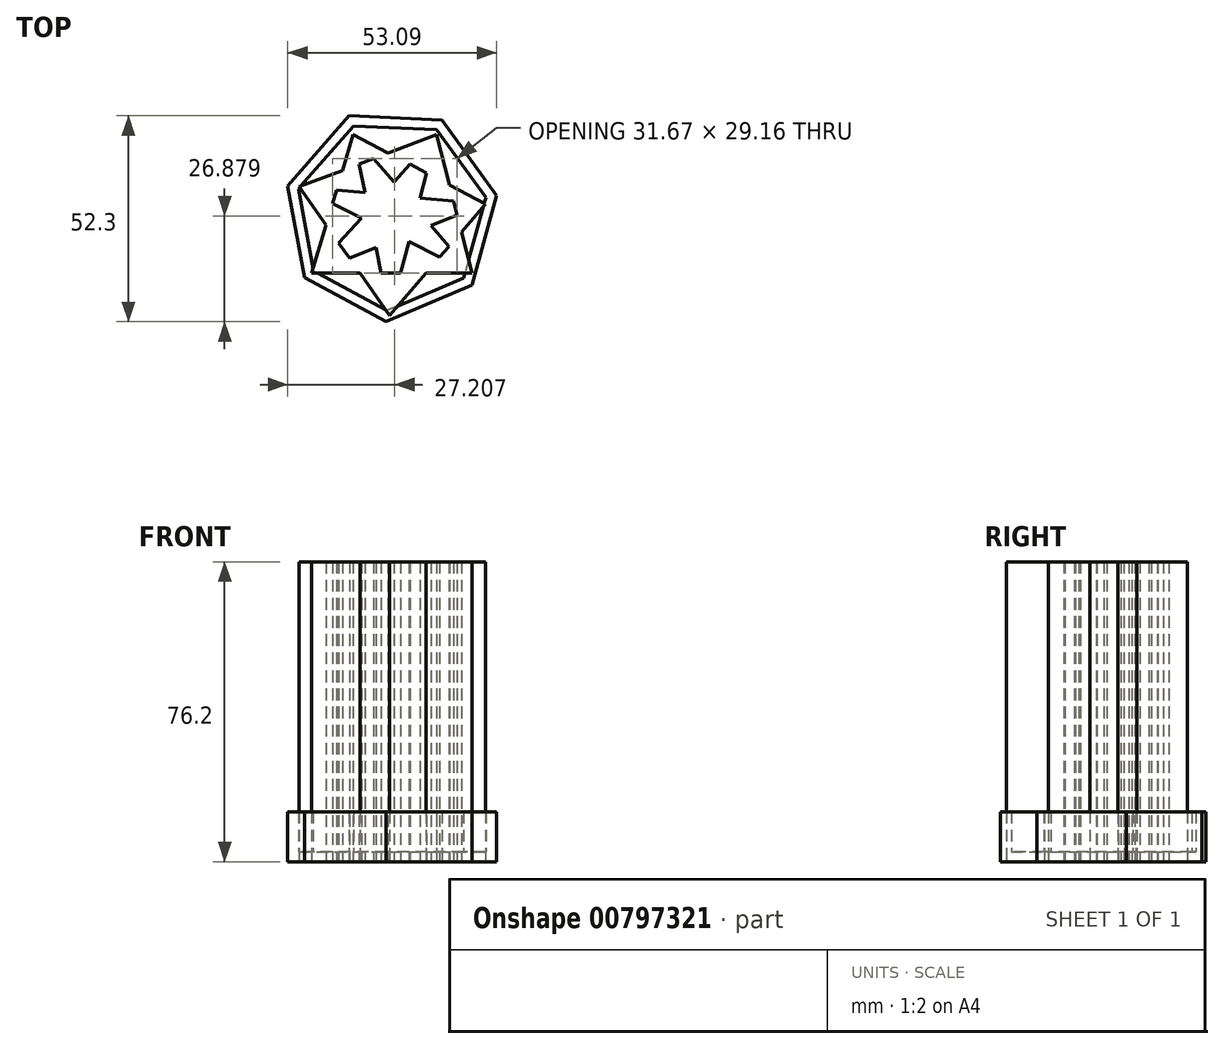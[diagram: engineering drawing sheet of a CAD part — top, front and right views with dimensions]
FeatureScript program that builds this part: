
annotation { "Feature Type Name" : "Feature", "Feature Type Description" : "" }
export const myFeature = defineFeature(function(context is Context, id is Id, definition is map)
    precondition{}
    {
        {
            var Q0;
            Q0=qCreatedBy(makeId("Top.planeOp"),FACE);
            var sketch = newSketch(context, id + "F0", { "sketchPlane" : qUnion([Q0])});
            skCircle(sketch, "E0.cCircle", {"center": v(-20.52, 14.93) * mm, "radius": 27.26 * mm, "construction": true});
            skLineSegment(sketch, "E0.0", {"start": v(0, -3.02) * mm, "end": v(-21.75, -12.3) * mm});
            skLineSegment(sketch, "E0.1", {"start": v(-21.75, -12.3) * mm, "end": v(-42.58, -1.08) * mm});
            skLineSegment(sketch, "E0.2", {"start": v(-42.58, -1.08) * mm, "end": v(-46.79, 22.2) * mm});
            skLineSegment(sketch, "E0.3", {"start": v(-46.79, 22.2) * mm, "end": v(-31.22, 40) * mm});
            skLineSegment(sketch, "E0.4", {"start": v(-31.22, 40) * mm, "end": v(-7.59, 38.92) * mm});
            skLineSegment(sketch, "E0.5", {"start": v(-7.59, 38.92) * mm, "end": v(6.3, 19.78) * mm});
            skLineSegment(sketch, "E0.6", {"start": v(6.3, 19.78) * mm, "end": v(0, -3.02) * mm});
            skSolve(sketch);
        }
        {
            var Q0;
            Q0=makeQuery(id+"F0.imprint","IMPRINT",FACE,{"disambiguationData":[TD([[makeQuery(id+"F0.imprint","IMPRINT",EDGE,{"derivedFrom":sQuery(id+"F0.wireOp",EDGE,"E0.0")}),-1.0]])]});
            extrude(context, id + "F1", {"entities" : qUnion([Q0]), "depth" : 12.7 * mm, "offsetDistance" : 25.4 * mm});
        }
        {
            var Q0;
            Q0=makeQuery(id+"F1.opExtrude","CAP_FACE",FACE,{"disambiguationData":[OSD([sQuery(id+"F0.wireOp",EDGE,"E0.0"),sQuery(id+"F0.wireOp",EDGE,"E0.1"),sQuery(id+"F0.wireOp",EDGE,"E0.2"),sQuery(id+"F0.wireOp",EDGE,"E0.3"),sQuery(id+"F0.wireOp",EDGE,"E0.4"),sQuery(id+"F0.wireOp",EDGE,"E0.5"),sQuery(id+"F0.wireOp",EDGE,"E0.6")])],"isStart":false});
            shell(context, id + "F2", {"entities" : qUnion([Q0]), "thickness" : 2.54 * mm});
        }
        {
            var Q0;
            Q0=qCreatedBy(makeId("Top.planeOp"),FACE);
            var sketch = newSketch(context, id + "F3", { "sketchPlane" : qUnion([Q0])});
            skLineSegment(sketch, "E1", {"start": v(-30.16, 35.24) * mm, "end": v(-20.88, -10.71) * mm});
            skLineSegment(sketch, "E2", {"start": v(-40.76, 0) * mm, "end": v(0, 0) * mm});
            skLineSegment(sketch, "E3", {"start": v(0, 0) * mm, "end": v(-8.95, 35.24) * mm});
            skLineSegment(sketch, "E4", {"start": v(-8.95, 35.24) * mm, "end": v(-43.85, 21.98) * mm});
            skLineSegment(sketch, "E5", {"start": v(-43.85, 21.98) * mm, "end": v(-20.88, -10.71) * mm});
            skLineSegment(sketch, "E6", {"start": v(-20.88, -10.71) * mm, "end": v(3.42, 17.62) * mm});
            skPoint(sketch, "E6.endSnap0", {"position": v(-4.47, 17.62) * mm});
            skLineSegment(sketch, "E7", {"start": v(3.42, 17.62) * mm, "end": v(-40.76, 0) * mm});
            skLineSegment(sketch, "E8", {"start": v(-8.95, 35.24) * mm, "end": v(-40.76, 0) * mm});
            skLineSegment(sketch, "E9", {"start": v(-30.16, 35.24) * mm, "end": v(3.42, 17.62) * mm});
            skLineSegment(sketch, "E10", {"start": v(-8.95, 35.24) * mm, "end": v(-20.88, -10.71) * mm});
            skLineSegment(sketch, "E11", {"start": v(0, 0) * mm, "end": v(-43.85, 21.98) * mm});
            skLineSegment(sketch, "E12", {"start": v(3.42, 17.62) * mm, "end": v(-43.85, 21.98) * mm});
            skLineSegment(sketch, "E13", {"start": v(-40.76, 0) * mm, "end": v(-30.16, 35.24) * mm});
            skLineSegment(sketch, "E14", {"start": v(0, 0) * mm, "end": v(-30.16, 35.24) * mm});
            skSolve(sketch);
        }
        {
            var Q0;
            Q0 = qSketchRegion(id + "F3", true);
            extrude(context, id + "F4", {"entities" : qUnion([Q0]), "surfaceOperationType" : NewSurfaceOperationType.ADD, "depth" : 76.2 * mm, "offsetDistance" : 25.4 * mm});
        }
    });
